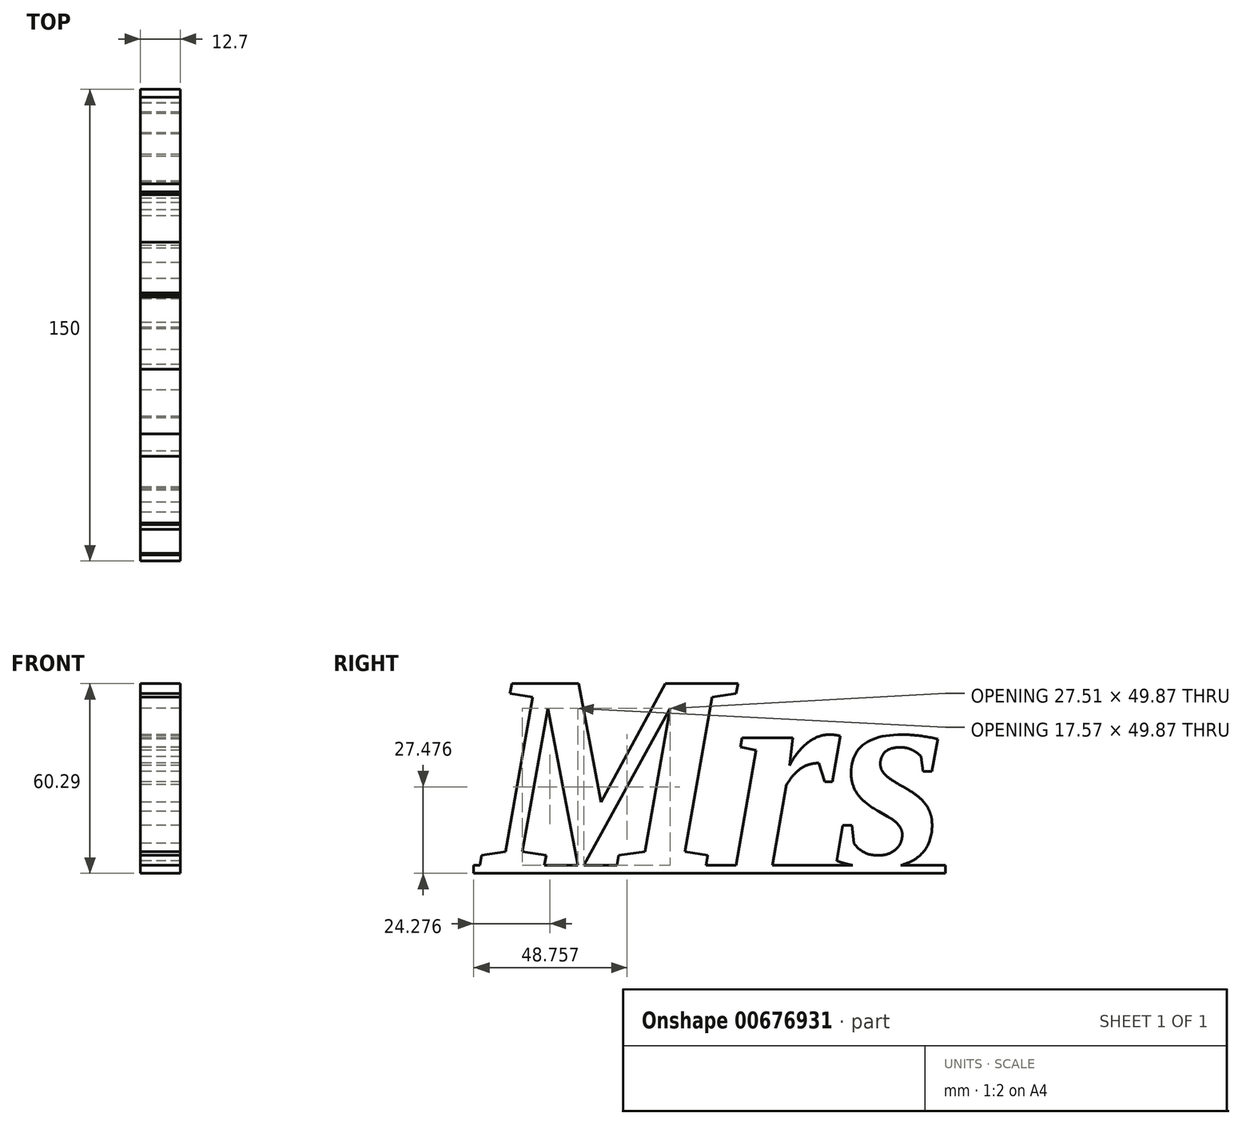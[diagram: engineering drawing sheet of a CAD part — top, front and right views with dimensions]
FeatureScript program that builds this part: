
annotation { "Feature Type Name" : "Feature", "Feature Type Description" : "" }
export const myFeature = defineFeature(function(context is Context, id is Id, definition is map)
    precondition{}
    {
        {
            var Q0;
            Q0=qCreatedBy(makeId("Right.planeOp"),FACE);
            var sketch = newSketch(context, id + "F0", { "sketchPlane" : qUnion([Q0])});
            skLineSegment(sketch, "E0.bottom", {"start": v(69.6, -2.54) * mm, "end": v(-80.4, -2.54) * mm});
            skLineSegment(sketch, "E0.top", {"start": v(69.6, 0) * mm, "end": v(-80.4, 0) * mm});
            skLineSegment(sketch, "E0.left", {"start": v(69.6, -2.54) * mm, "end": v(69.6, 0) * mm});
            skLineSegment(sketch, "E0.right", {"start": v(-80.4, -2.54) * mm, "end": v(-80.4, 0) * mm});
            skSolve(sketch);
        }
        {
            var Q0;
            Q0 = qSketchRegion(id + "F0", true);
            extrude(context, id + "F1", {"entities" : qUnion([Q0]), "endBound" : BoundingType.SYMMETRIC, "oppositeDirection" : true, "depth" : 12.7 * mm, "offsetDistance" : 25.4 * mm});
        }
        {
            var Q0;
            Q0=qCreatedBy(makeId("Right.planeOp"),FACE);
            var sketch = newSketch(context, id + "F2", { "sketchPlane" : qUnion([Q0])});
            skText(sketch, "E1", { "text": "Mrs", "fontName": "Tinos-BoldItalic.ttf"});
            const initialGuessF2  = {"E1": [-0.07726, 0, 1, 0, 0.0635]};
            skSetInitialGuess(sketch, initialGuessF2);
            skSolve(sketch);
        }
        {
            var Q0;
            Q0 = qSketchRegion(id + "F2", true);
            extrude(context, id + "F3", {"entities" : qUnion([Q0]), "operationType" : NewBodyOperationType.ADD, "endBound" : BoundingType.SYMMETRIC, "depth" : 12.7 * mm, "offsetDistance" : 25.4 * mm});
        }
    });
